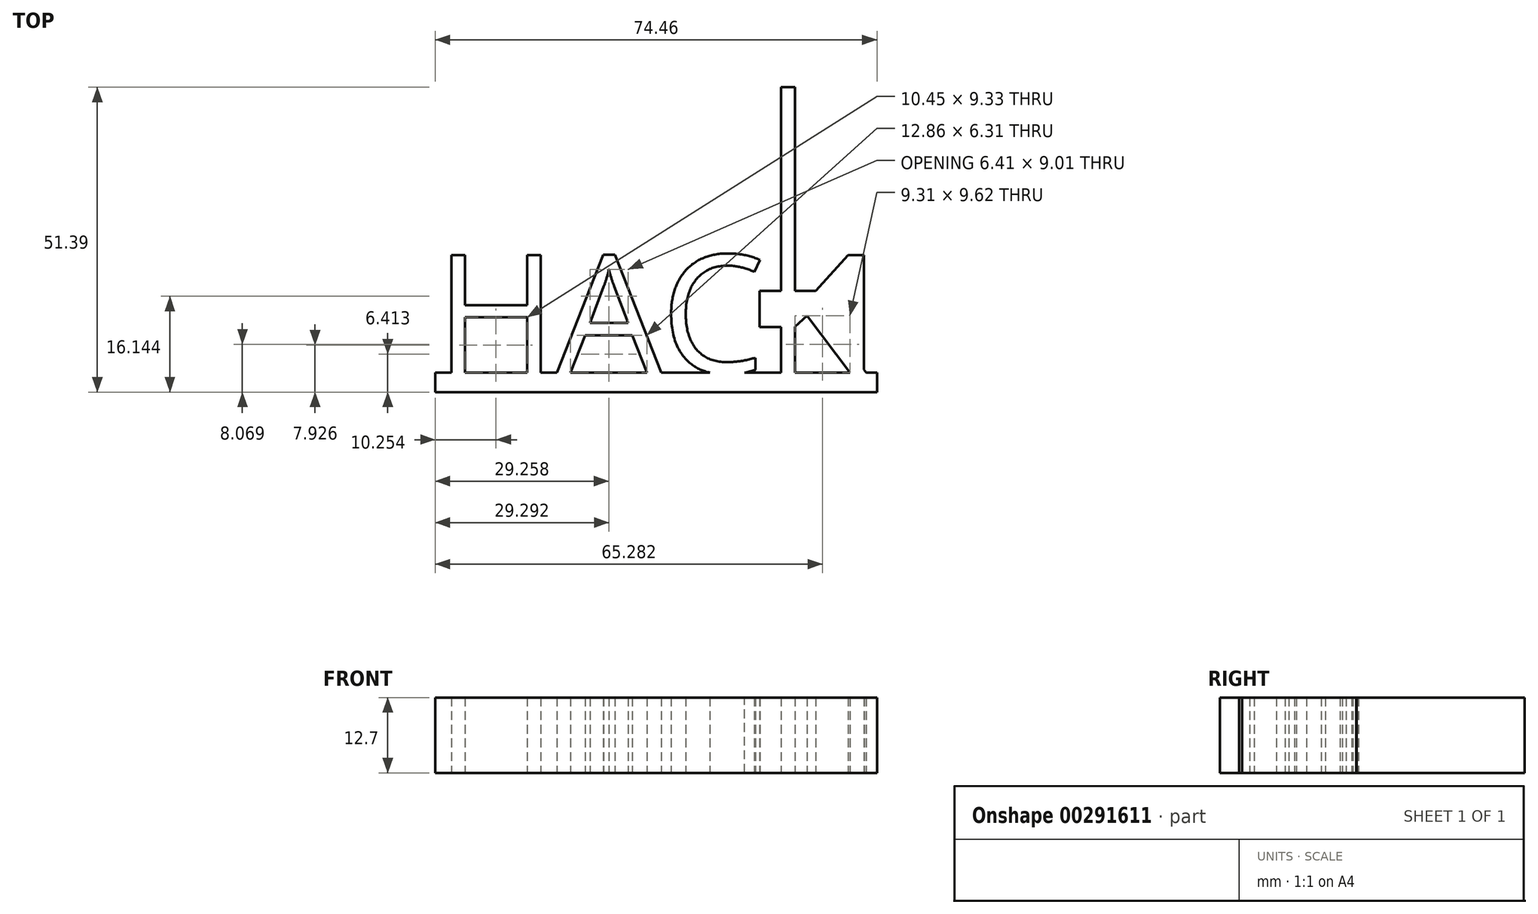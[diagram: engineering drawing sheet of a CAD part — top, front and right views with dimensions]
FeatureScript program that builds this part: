
annotation { "Feature Type Name" : "Feature", "Feature Type Description" : "" }
export const myFeature = defineFeature(function(context is Context, id is Id, definition is map)
    precondition{}
    {
        {
            var Q0;
            Q0=qCreatedBy(makeId("Top.planeOp"),FACE);
            var sketch = newSketch(context, id + "F0", { "sketchPlane" : qUnion([Q0])});
            skText(sketch, "E0", { "text": "HACK", "fontName": "OpenSans-Regular.ttf"});
            skLineSegment(sketch, "E1.bottom", {"start": v(-37.23, 0) * mm, "end": v(37.23, 0) * mm});
            skLineSegment(sketch, "E1.top", {"start": v(-37.23, -3.26) * mm, "end": v(37.23, -3.26) * mm});
            skLineSegment(sketch, "E1.left", {"start": v(-37.23, 0) * mm, "end": v(-37.23, -3.26) * mm});
            skLineSegment(sketch, "E1.right", {"start": v(37.23, 0) * mm, "end": v(37.23, -3.26) * mm});
            skLineSegment(sketch, "E2", {"start": v(35.02, 20) * mm, "end": v(35.02, 0) * mm});
            skLineSegment(sketch, "E3.bottom", {"start": v(23.4, 19.14) * mm, "end": v(21.04, 19.14) * mm});
            skLineSegment(sketch, "E3.top", {"start": v(23.4, 48.13) * mm, "end": v(21.04, 48.13) * mm});
            skLineSegment(sketch, "E3.left", {"start": v(23.4, 19.14) * mm, "end": v(23.4, 48.13) * mm});
            skLineSegment(sketch, "E3.right", {"start": v(21.04, 19.14) * mm, "end": v(21.04, 48.13) * mm});
            skLineSegment(sketch, "E4.bottom", {"start": v(27.04, 13.82) * mm, "end": v(17.47, 13.82) * mm});
            skLineSegment(sketch, "E4.top", {"start": v(27.04, 7.72) * mm, "end": v(17.47, 7.72) * mm});
            skLineSegment(sketch, "E4.left", {"start": v(27.04, 13.82) * mm, "end": v(27.04, 7.72) * mm});
            skLineSegment(sketch, "E4.right", {"start": v(17.47, 13.82) * mm, "end": v(17.47, 7.72) * mm});
            const initialGuessF0  = {"E0": [-0.03723, 0, 1, 0, 0.02]};
            skSetInitialGuess(sketch, initialGuessF0);
            skSolve(sketch);
        }
        {
            var Q0;
            Q0 = qSketchRegion(id + "F0", true);
            extrude(context, id + "F1", {"entities" : qUnion([Q0]), "depth" : 12.7 * mm});
        }
    });
